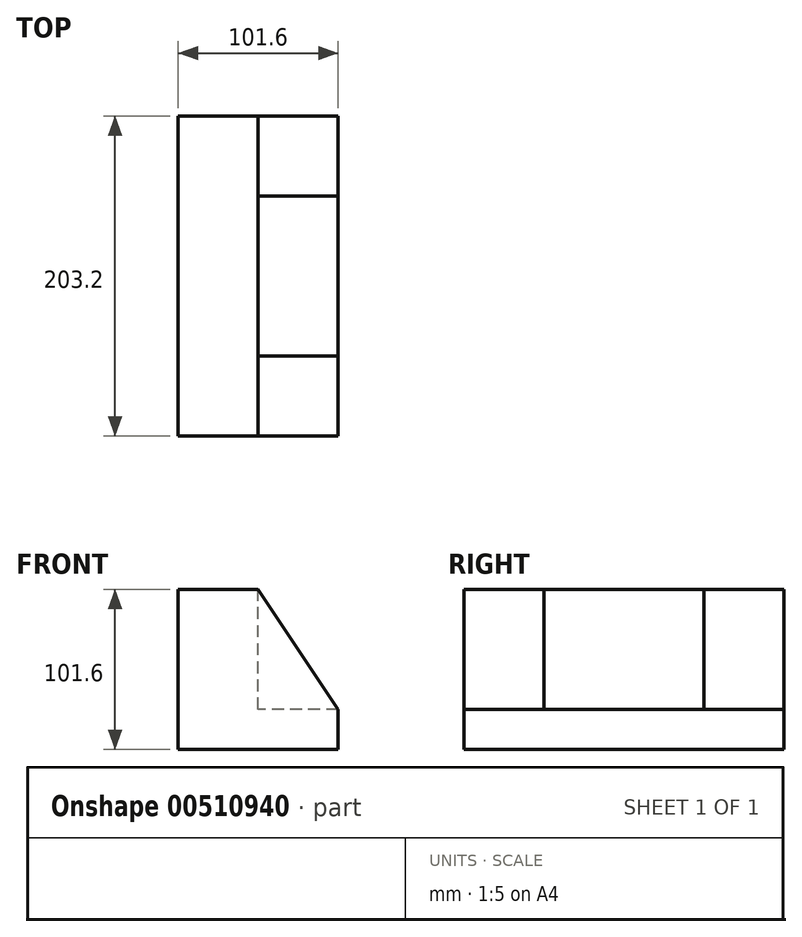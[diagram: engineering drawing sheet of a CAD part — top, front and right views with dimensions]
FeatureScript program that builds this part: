
annotation { "Feature Type Name" : "Feature", "Feature Type Description" : "" }
export const myFeature = defineFeature(function(context is Context, id is Id, definition is map)
    precondition{}
    {
        {
            var Q0;
            Q0=qCreatedBy(makeId("Top.planeOp"),FACE);
            var sketch = newSketch(context, id + "F0", { "sketchPlane" : qUnion([Q0])});
            skLineSegment(sketch, "E0.bottom", {"start": v(0, 0) * mm, "end": v(-101.6, 0) * mm});
            skLineSegment(sketch, "E0.top", {"start": v(0, -203.2) * mm, "end": v(-101.6, -203.2) * mm});
            skLineSegment(sketch, "E0.left", {"start": v(0, 0) * mm, "end": v(0, -203.2) * mm});
            skLineSegment(sketch, "E0.right", {"start": v(-101.6, 0) * mm, "end": v(-101.6, -203.2) * mm});
            skSolve(sketch);
        }
        {
            var Q0;
            Q0 = qSketchRegion(id + "F0", true);
            extrude(context, id + "F1", {"entities" : qUnion([Q0]), "depth" : 101.6 * mm});
        }
        {
            var Q0;
            Q0=makeQuery(id+"F1.opExtrude","CAP_FACE",FACE,{"disambiguationData":[OSD([sQuery(id+"F0.wireOp",EDGE,"E0.bottom"),sQuery(id+"F0.wireOp",EDGE,"E0.top"),sQuery(id+"F0.wireOp",EDGE,"E0.left"),sQuery(id+"F0.wireOp",EDGE,"E0.right")])],"isStart":false});
            var sketch = newSketch(context, id + "F2", { "sketchPlane" : qUnion([Q0])});
            skLineSegment(sketch, "E1.bottom", {"start": v(0, -203.2) * mm, "end": v(-50.8, -203.2) * mm});
            skLineSegment(sketch, "E1.top", {"start": v(0, 0) * mm, "end": v(-50.8, 0) * mm});
            skLineSegment(sketch, "E1.left", {"start": v(0, -203.2) * mm, "end": v(0, 0) * mm});
            skLineSegment(sketch, "E1.right", {"start": v(-50.8, -203.2) * mm, "end": v(-50.8, 0) * mm});
            skSolve(sketch);
        }
        {
            var Q0;
            Q0=makeQuery(id+"F2.imprint","IMPRINT",FACE,{"disambiguationData":[TD([[makeQuery(id+"F2.imprint","IMPRINT",EDGE,{"derivedFrom":sQuery(id+"F2.wireOp",EDGE,"E1.bottom")}),-1.0]])]});
            extrude(context, id + "F3", {"entities" : qUnion([Q0]), "operationType" : NewBodyOperationType.REMOVE, "oppositeDirection" : true, "depth" : 76.2 * mm});
        }
        {
            var Q0;
            Q0=makeQuery(id+"F1.opExtrude","SWEPT_FACE",FACE,{"disambiguationData":[OSD([sQuery(id+"F0.wireOp",EDGE,"E0.bottom")])]});
            var sketch = newSketch(context, id + "F4", { "sketchPlane" : qUnion([Q0])});
            skLineSegment(sketch, "E2", {"start": v(50.8, 101.6) * mm, "end": v(0, 25.4) * mm});
            skSolve(sketch);
        }
        {
            var Q0;
            Q0=makeQuery(id+"F4.imprint","IMPRINT",FACE,{"disambiguationData":[TD([[makeQuery(id+"F4.imprint","IMPRINT",EDGE,{"derivedFrom":sQuery(id+"F4.wireOp",EDGE,"E2")}),1.0]])]});
            extrude(context, id + "F5", {"entities" : qUnion([Q0]), "operationType" : NewBodyOperationType.ADD, "oppositeDirection" : true, "depth" : 50.8 * mm});
        }
        {
            var Q0;
            Q0=makeQuery(id+"F1.opExtrude","SWEPT_FACE",FACE,{"disambiguationData":[OSD([sQuery(id+"F0.wireOp",EDGE,"E0.top")])]});
            var sketch = newSketch(context, id + "F6", { "sketchPlane" : qUnion([Q0])});
            skLineSegment(sketch, "E3", {"start": v(-50.8, 101.6) * mm, "end": v(0, 25.4) * mm});
            skSolve(sketch);
        }
        {
            var Q0;
            Q0=makeQuery(id+"F6.imprint","IMPRINT",FACE,{"disambiguationData":[TD([[makeQuery(id+"F6.imprint","IMPRINT",EDGE,{"derivedFrom":sQuery(id+"F6.wireOp",EDGE,"E3")}),-1.0]])]});
            extrude(context, id + "F7", {"entities" : qUnion([Q0]), "operationType" : NewBodyOperationType.ADD, "oppositeDirection" : true, "depth" : 50.8 * mm});
        }
    });
